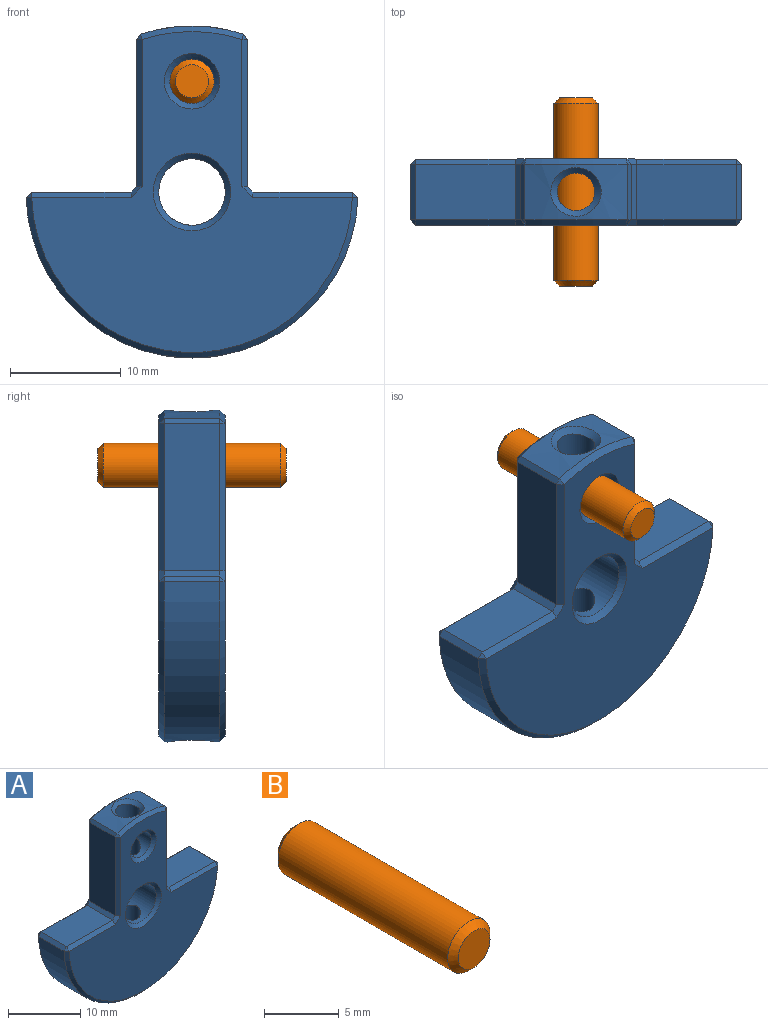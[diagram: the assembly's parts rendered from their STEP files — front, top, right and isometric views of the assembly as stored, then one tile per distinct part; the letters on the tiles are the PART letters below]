
ASSEMBLY  parts=2 mates=2
PART A: 49 faces, bbox 30x6x30 mm
  f0: plane 29x28.98mm, normal (0,-1,0), area 391.5mm2, adj f15,f17,f18,f27,f28,f37,f38,f41
  f1: plane 29x28.98mm, normal (0,1,0), area 391.5mm2, adj f16,f20,f21,f30,f31,f39,f40,f42
  f2: cylinder r=15mm len=29.98mm, axis (0,1,0), area 214.8mm2, adj f13,f19,f28,f29,f30
  f3: cylinder r=15mm len=9.31mm, axis (0,1,0), area 31.6mm2, adj f22,f27,f31,f32,f44
  f4: cylinder r=3mm len=6mm, axis (0,-1,0), area 75.2mm2, adj f11,f12,f46,f48
  f5: cylinder r=2mm len=5mm, axis (0,-1,0), area 42.3mm2, adj f10,f11,f45,f47
  f6: plane 8.99x5mm, normal (0,0,1), area 45mm2, adj f29,f38,f39,f43
  f7: plane 8.99x5mm, normal (0,0,1), area 45mm2, adj f14,f18,f19,f20
  f8: plane 13.28x5mm, normal (1,0,0), area 66.4mm2, adj f14,f17,f21,f22
  f9: plane 13.28x5mm, normal (-1,0,0), area 66.4mm2, adj f32,f37,f40,f43
  f10: cylinder r=1.7mm len=3.4mm, axis (0,0,1), area 35mm2, adj f5,f44
  f11: cylinder r=1.7mm len=6.47mm, axis (0,0,1), area 61.6mm2, adj f4,f5
  f12: cylinder r=1.7mm len=11.86mm, axis (0,0,1), area 122.5mm2, adj f4,f13
  f13: bspline ~4.55x4.4mm, area 9.1mm2, adj f2,f12
  f14: plane 5x0.5mm, normal (0.71,0,0.71), area 3.5mm2, adj f7,f8,f15,f16
  f15: plane 1x1mm, normal (0.58,-0.58,0.58), area 0.6mm2, adj f0,f14,f17,f18
  f16: plane 1x1mm, normal (0.58,0.58,0.58), area 0.6mm2, adj f1,f14,f20,f21
  f17: plane 13.28x0.5mm, normal (0.71,-0.71,0), area 9.4mm2, adj f0,f8,f15,f23
  f18: plane 8.99x0.5mm, normal (0,-0.71,0.71), area 6.4mm2, adj f0,f7,f15,f24
  f19: plane 5x0.52mm, normal (0.72,0,0.69), area 3.6mm2, adj f2,f7,f24,f25
  f20: plane 8.99x0.5mm, normal (0,0.71,0.71), area 6.4mm2, adj f1,f7,f16,f25
  f21: plane 13.28x0.5mm, normal (0.71,0.71,0), area 9.4mm2, adj f1,f8,f16,f26
  f22: plane 5x0.48mm, normal (0.81,0,0.59), area 2.9mm2, adj f3,f8,f23,f26
  f23: plane 0.5x0.5mm, normal (0.63,-0.63,0.46), area 0.2mm2, adj f17,f22,f27
  f24: plane 0.52x0.5mm, normal (0.59,-0.57,0.57), area 0.2mm2, adj f18,f19,f28
  f25: plane 0.52x0.5mm, normal (0.59,0.57,0.57), area 0.2mm2, adj f19,f20,f30
  f26: plane 0.5x0.5mm, normal (0.63,0.63,0.46), area 0.2mm2, adj f21,f22,f31
  f27: cone r=14.5mm half-angle=45deg, axis (0,1,0), area 6.6mm2, adj f0,f3,f23,f33
  f28: cone r=14.5mm half-angle=45deg, axis (0,1,0), area 32mm2, adj f0,f2,f24,f34
  f29: plane 5x0.52mm, normal (-0.72,0,0.69), area 3.6mm2, adj f2,f6,f34,f35
  f30: cone r=15mm half-angle=45deg, axis (0,-1,0), area 32mm2, adj f1,f2,f25,f35
  f31: cone r=15mm half-angle=45deg, axis (0,-1,0), area 6.6mm2, adj f1,f3,f26,f36
  f32: plane 5x0.48mm, normal (-0.81,0,0.59), area 2.9mm2, adj f3,f9,f33,f36
  f33: plane 0.5x0.5mm, normal (-0.63,-0.63,0.46), area 0.2mm2, adj f27,f32,f37
  f34: plane 0.52x0.5mm, normal (-0.59,-0.57,0.57), area 0.2mm2, adj f28,f29,f38
  f35: plane 0.52x0.5mm, normal (-0.59,0.57,0.57), area 0.2mm2, adj f29,f30,f39
  f36: plane 0.5x0.5mm, normal (-0.63,0.63,0.46), area 0.2mm2, adj f31,f32,f40
  f37: plane 13.28x0.5mm, normal (-0.71,-0.71,0), area 9.4mm2, adj f0,f9,f33,f41
  f38: plane 8.99x0.5mm, normal (0,-0.71,0.71), area 6.4mm2, adj f0,f6,f34,f41
  f39: plane 8.99x0.5mm, normal (0,0.71,0.71), area 6.4mm2, adj f1,f6,f35,f42
  f40: plane 13.28x0.5mm, normal (-0.71,0.71,0), area 9.4mm2, adj f1,f9,f36,f42
  f41: plane 1x1mm, normal (-0.58,-0.58,0.58), area 0.6mm2, adj f0,f37,f38,f43
  f42: plane 1x1mm, normal (-0.58,0.58,0.58), area 0.6mm2, adj f1,f39,f40,f43
  f43: plane 5x0.5mm, normal (-0.71,0,0.71), area 3.5mm2, adj f6,f9,f41,f42
  f44: bspline ~4.55x4.4mm, area 9.1mm2, adj f3,f10
  f45: cone r=2mm half-angle=45deg, axis (0,1,0), area 10mm2, adj f1,f5
  f46: cone r=3mm half-angle=45deg, axis (0,1,0), area 14.4mm2, adj f1,f4
  f47: cone r=2mm half-angle=45deg, axis (0,-1,0), area 10mm2, adj f0,f5
  f48: cone r=3mm half-angle=45deg, axis (0,-1,0), area 14.4mm2, adj f0,f4
PART B: 5 faces, bbox 4x17x4 mm
  f0: cylinder r=2mm len=16mm, axis (0,1,0), area 201.1mm2, adj f3,f4
  f1: plane 3x3mm, normal (0,-1,0), area 7.1mm2, adj f4
  f2: plane 3x3mm, normal (0,1,0), area 7.1mm2, adj f3
  f3: cone r=2mm half-angle=45deg, axis (0,-1,0), area 7.8mm2, adj f0,f2
  f4: cone r=1.5mm half-angle=45deg, axis (0,1,0), area 7.8mm2, adj f0,f1
PLACE A t=(-14.74,-0.52,-5.82)mm
PLACE B t=(-55.49,4.98,-45.43)mm
MATE cylindrical A.f5 <-> B.f0  axis (0,-1,0) through (-14.74,-6.02,4.18)mm
MATE planar B.f0 <-> A.f5  axis (0,1,0) through (-14.74,4.98,4.18)mm
